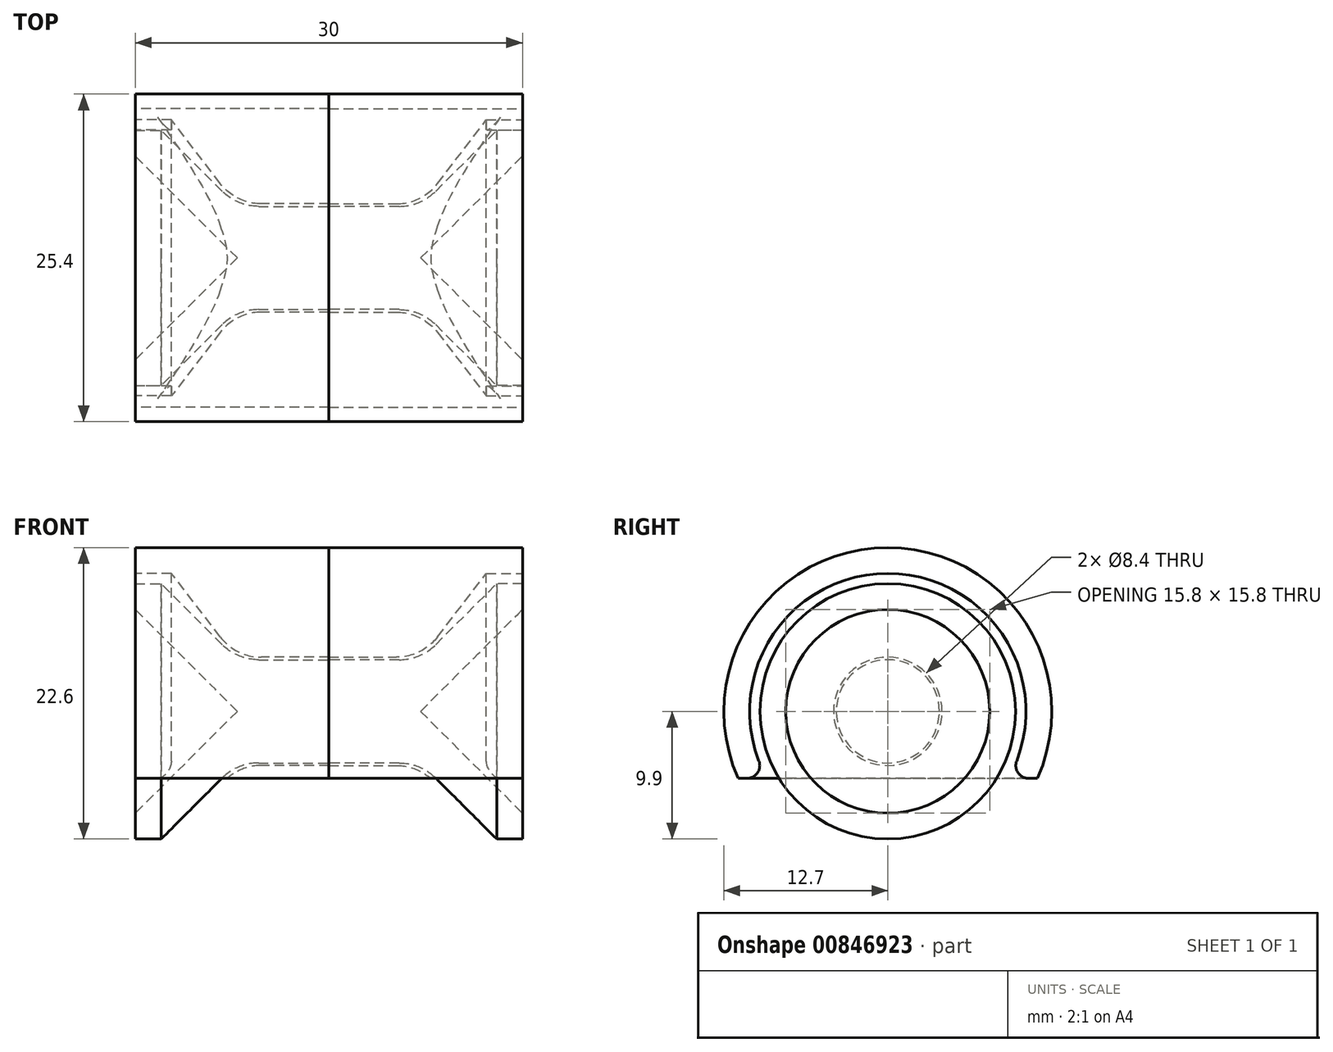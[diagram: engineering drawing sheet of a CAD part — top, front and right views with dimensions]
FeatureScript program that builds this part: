
annotation { "Feature Type Name" : "Feature", "Feature Type Description" : "" }
export const myFeature = defineFeature(function(context is Context, id is Id, definition is map)
    precondition{}
    {
        {
            assignVariable(context, id + "F0", {"name" : "overfill", "anyValue" : .1 * mm});
        }
        {
            assignVariable(context, id + "F1", {"name" : "r_wheel", "anyValue" : 10 * mm});
        }
        {
            assignVariable(context, id + "F2", {"name" : "dr_axle_gap", "anyValue" : .1 * mm});
        }
        {
            assignVariable(context, id + "F3", {"name" : "dr_wheel_gap", "anyValue" : .5 * mm + getVariable(context, 'dr_axle_gap')});
        }
        {
            assignVariable(context, id + "F4", {"name" : "r_wheel_oo", "anyValue" : getVariable(context, 'r_wheel') + getVariable(context, 'dr_wheel_gap') + getVariable(context, 'overfill')});
        }
        {
            assignVariable(context, id + "F5", {"name" : "z_frame_top", "anyValue" : getVariable(context, 'r_wheel_oo') + 2 * mm});
        }
        {
            var Q0;
            Q0=qCreatedBy(makeId("Front.planeOp"),FACE);
            var sketch = newSketch(context, id + "F6", { "sketchPlane" : qUnion([Q0])});
            skLineSegment(sketch, "E0", {"start": v(0, 0) * mm, "end": v(-7.1, 0) * mm});
            skLineSegment(sketch, "E1", {"start": v(-7.1, 0) * mm, "end": v(-15, 7.9) * mm});
            skLineSegment(sketch, "E2", {"start": v(-15, 7.9) * mm, "end": v(-15, 9.9) * mm});
            skLineSegment(sketch, "E3", {"start": v(-15, 9.9) * mm, "end": v(-13, 9.9) * mm});
            skLineSegment(sketch, "E4", {"start": v(-13, 9.9) * mm, "end": v(-8.27, 5.17) * mm});
            skLineSegment(sketch, "E5", {"start": v(-5.44, 4) * mm, "end": v(0, 4) * mm});
            skLineSegment(sketch, "E6", {"start": v(0, 4) * mm, "end": v(0, 0) * mm});
            skPoint(sketch, "E7.visualSharp", {"position": v(-7.1, 4) * mm});
            skArc(sketch, "E7.filletArc", {"start": v(-8.27, 5.17) * mm, "mid": v(-6.97, 4.3) * mm, "end": v(-5.44, 4) * mm});
            skLineSegment(sketch, "E8", {"start": v(-15, 9.9) * mm, "end": v(-15, 18.17) * mm, "construction": true});
            skSolve(sketch);
        }
        {
            var Q0;
            Q0=makeQuery(id+"F6.imprint","IMPRINT",FACE,{"disambiguationData":[TD([[makeQuery(id+"F6.imprint","IMPRINT",EDGE,{"derivedFrom":sQuery(id+"F6.wireOp",EDGE,"E0")}),-1.0]])]});
            var sketch = newSketch(context, id + "F7", { "sketchPlane" : qUnion([Q0])});
            skLineSegment(sketch, "E9", {"start": v(-15, 10.7) * mm, "end": v(-12.2, 10.7) * mm});
            skLineSegment(sketch, "E10", {"start": v(-12.2, 10.7) * mm, "end": v(-8.42, 5.77) * mm});
            skLineSegment(sketch, "E11", {"start": v(-5.24, 4.2) * mm, "end": v(0, 4.2) * mm});
            skLineSegment(sketch, "E12", {"start": v(0, 4.2) * mm, "end": v(0, 0) * mm});
            skLineSegment(sketch, "E13", {"start": v(0, 0) * mm, "end": v(-15, 0) * mm});
            skLineSegment(sketch, "E14", {"start": v(-15, 0) * mm, "end": v(-15, 10.7) * mm});
            skPoint(sketch, "E15.visualSharp", {"position": v(-7.22, 4.2) * mm});
            skArc(sketch, "E15.filletArc", {"start": v(-8.42, 5.77) * mm, "mid": v(-7.01, 4.61) * mm, "end": v(-5.24, 4.2) * mm});
            skLineSegment(sketch, "E16", {"start": v(-13, 9.9) * mm, "end": v(-12.2, 10.7) * mm, "construction": true});
            skPoint(sketch, "E17.0", {"position": v(-5.44, 4) * mm});
            skLineSegment(sketch, "E18", {"start": v(-5.44, 4) * mm, "end": v(-5.24, 4.2) * mm, "construction": true});
            skSolve(sketch);
        }
        {
            var Q0;
            {var subQ4=sQuery(id+"F7.wireOp",EDGE,"E9");Q0=makeQuery(id+"F7.imprint","IMPRINT",FACE,{"disambiguationData":[TD([[makeQuery(id+"F7.imprint","IMPRINT",EDGE,{"derivedFrom":subQ4}),-1.0]])]});}
            var sketch = newSketch(context, id + "F8", { "sketchPlane" : qUnion([Q0])});
            skPoint(sketch, "E19.0", {"position": v(-15, 0) * mm});
            skPoint(sketch, "E20.0", {"position": v(-15, 10.7) * mm});
            skLineSegment(sketch, "E21.bottom", {"start": v(-15, 0) * mm, "end": v(0, 0) * mm});
            skLineSegment(sketch, "E21.top", {"start": v(-15, 12.7) * mm, "end": v(0, 12.7) * mm});
            skLineSegment(sketch, "E21.left", {"start": v(-15, 0) * mm, "end": v(-15, 12.7) * mm});
            skLineSegment(sketch, "E21.right", {"start": v(0, 0) * mm, "end": v(0, 12.7) * mm});
            skSolve(sketch);
        }
        {
            var Q0;
            {var subQ1=makeQuery(id+"F6.imprint","IMPRINT",EDGE,{"derivedFrom":sQuery(id+"F6.wireOp",EDGE,"E1")});Q0=makeQuery(id+"F7.imprint","IMPRINT",FACE,{"disambiguationData":[TD([[makeQuery(id+"F7.imprint","IMPRINT",EDGE,{"derivedFrom":subQ1}),1.0]])]});}
            var sketch = newSketch(context, id + "F9", { "sketchPlane" : qUnion([Q0])});
            skLineSegment(sketch, "E22.bottom", {"start": v(-15, -5.2) * mm, "end": v(0, -5.2) * mm});
            skLineSegment(sketch, "E22.top", {"start": v(-15, -12.7) * mm, "end": v(0, -12.7) * mm});
            skLineSegment(sketch, "E22.left", {"start": v(-15, -5.2) * mm, "end": v(-15, -12.7) * mm});
            skLineSegment(sketch, "E22.right", {"start": v(0, -5.2) * mm, "end": v(0, -12.7) * mm});
            skLineSegment(sketch, "E23", {"start": v(-15, 0) * mm, "end": v(-15, -5.2) * mm, "construction": true});
            skLineSegment(sketch, "E24", {"start": v(0, 0) * mm, "end": v(0, -5.2) * mm, "construction": true});
            skSolve(sketch);
        }
        {
            var Q0;
            {var subQ2=sQuery(id+"F8.wireOp",EDGE,"E21.top");Q0=makeQuery(id+"F8.imprint","IMPRINT",FACE,{"disambiguationData":[TD([[makeQuery(id+"F8.imprint","IMPRINT",EDGE,{"derivedFrom":subQ2}),-1.0]])]});}
            var Q1;
            Q1=sQuery(id+"F8.wireOp",EDGE,"E21.bottom");
            revolve(context, id + "F10", {"surfaceOperationType" : NewSurfaceOperationType.NEW, "entities" : qUnion([Q0]), "axis" : qUnion([Q1]), "revolveType" : RevolveType.FULL});
        }
        {
            var Q0;
            Q0 = qSketchRegion(id + "F9", true);
            extrude(context, id + "F11", {"entities" : qUnion([Q0]), "operationType" : NewBodyOperationType.REMOVE, "depth" : 2 * getVariable(context, 'z_frame_top'), "offsetDistance" : 25 * mm, "symmetric" : true});
        }
        {
            var Q0;
            Q0=makeQuery(id+"F6.imprint","IMPRINT",FACE,{"disambiguationData":[TD([[makeQuery(id+"F6.imprint","IMPRINT",EDGE,{"derivedFrom":sQuery(id+"F6.wireOp",EDGE,"E0")}),-1.0]])]});
            var Q1;
            Q1=sQuery(id+"F6.wireOp",EDGE,"E0");
            revolve(context, id + "F12", {"surfaceOperationType" : NewSurfaceOperationType.NEW, "entities" : qUnion([Q0]), "axis" : qUnion([Q1]), "revolveType" : RevolveType.FULL});
        }
        {
            var Q0;
            Q0=makeQuery(id+"F12.opRevolve","SWEPT_BODY",BODY,{"disambiguationData":[OSD([sQuery(id+"F6.wireOp",EDGE,"E0"),sQuery(id+"F6.wireOp",EDGE,"E1"),sQuery(id+"F6.wireOp",EDGE,"E2"),sQuery(id+"F6.wireOp",EDGE,"E3"),sQuery(id+"F6.wireOp",EDGE,"E4"),sQuery(id+"F6.wireOp",EDGE,"E5"),sQuery(id+"F6.wireOp",EDGE,"E6"),sQuery(id+"F6.wireOp",EDGE,"E7.filletArc")])]});
            var Q1;
            Q1=makeQuery(id+"F12.opRevolve","SWEPT_FACE",FACE,{"disambiguationData":[OSD([sQuery(id+"F6.wireOp",EDGE,"E6")])]});
            mirror(context, id + "F13", {"operationType" : NewBodyOperationType.ADD, "entities" : qUnion([Q0]), "mirrorPlane" : qUnion([Q1])});
        }
        {
            var Q0;
            Q0=makeQuery(id+"F10.opRevolve","SWEPT_BODY",BODY,{"disambiguationData":[OSD([sQuery(id+"F7.wireOp",EDGE,"E9"),sQuery(id+"F7.wireOp",EDGE,"E10"),sQuery(id+"F7.wireOp",EDGE,"E11"),sQuery(id+"F7.wireOp",EDGE,"E15.filletArc"),sQuery(id+"F8.wireOp",EDGE,"E21.top"),sQuery(id+"F8.wireOp",EDGE,"E21.left"),sQuery(id+"F8.wireOp",EDGE,"E21.right")])]});
            var Q1;
            Q1=makeQuery(id+"F10.opRevolve","SWEPT_FACE",FACE,{"disambiguationData":[OSD([sQuery(id+"F8.wireOp",EDGE,"E21.right")])]});
            mirror(context, id + "F14", {"operationType" : NewBodyOperationType.ADD, "entities" : qUnion([Q0]), "mirrorPlane" : qUnion([Q1])});
        }
        {
            var Q0;
            Q0=makeQuery(id+"F11.boolean.opBoolean","INTERSECT",EDGE,{"disambiguationData":[OD(0.0)],"derivedFrom":[makeQuery(id+"F10.opRevolve","SWEPT_FACE",FACE,{"disambiguationData":[OSD([sQuery(id+"F7.wireOp",EDGE,"E9")])]}),makeQuery(id+"F11.opExtrude","SWEPT_FACE",FACE,{"disambiguationData":[OSD([sQuery(id+"F9.wireOp",EDGE,"E22.bottom")])]})]});
            var Q1;
            Q1=makeQuery(id+"F11.boolean.opBoolean","INTERSECT",EDGE,{"disambiguationData":[OD(1.0)],"derivedFrom":[makeQuery(id+"F10.opRevolve","SWEPT_FACE",FACE,{"disambiguationData":[OSD([sQuery(id+"F7.wireOp",EDGE,"E9")])]}),makeQuery(id+"F11.opExtrude","SWEPT_FACE",FACE,{"disambiguationData":[OSD([sQuery(id+"F9.wireOp",EDGE,"E22.bottom")])]})]});
            var Q2;
            Q2=makeQuery(id+"F14.opPattern","COPY",EDGE,{"derivedFrom":makeQuery(id+"F11.boolean.opBoolean","INTERSECT",EDGE,{"disambiguationData":[OD(0.0)],"derivedFrom":[makeQuery(id+"F10.opRevolve","SWEPT_FACE",FACE,{"disambiguationData":[OSD([sQuery(id+"F7.wireOp",EDGE,"E9")])]}),makeQuery(id+"F11.opExtrude","SWEPT_FACE",FACE,{"disambiguationData":[OSD([sQuery(id+"F9.wireOp",EDGE,"E22.bottom")])]})]}),"instanceName":"1"});
            var Q3;
            Q3=makeQuery(id+"F14.opPattern","COPY",EDGE,{"derivedFrom":makeQuery(id+"F11.boolean.opBoolean","INTERSECT",EDGE,{"disambiguationData":[OD(1.0)],"derivedFrom":[makeQuery(id+"F10.opRevolve","SWEPT_FACE",FACE,{"disambiguationData":[OSD([sQuery(id+"F7.wireOp",EDGE,"E9")])]}),makeQuery(id+"F11.opExtrude","SWEPT_FACE",FACE,{"disambiguationData":[OSD([sQuery(id+"F9.wireOp",EDGE,"E22.bottom")])]})]}),"instanceName":"1"});
            fillet(context, id + "F15", {"entities" : qUnion([Q0, Q1, Q2, Q3]), "radius" : 1 * mm, "tangentPropagation" : true, "allowEdgeOverflow" : false});
        }
    });
